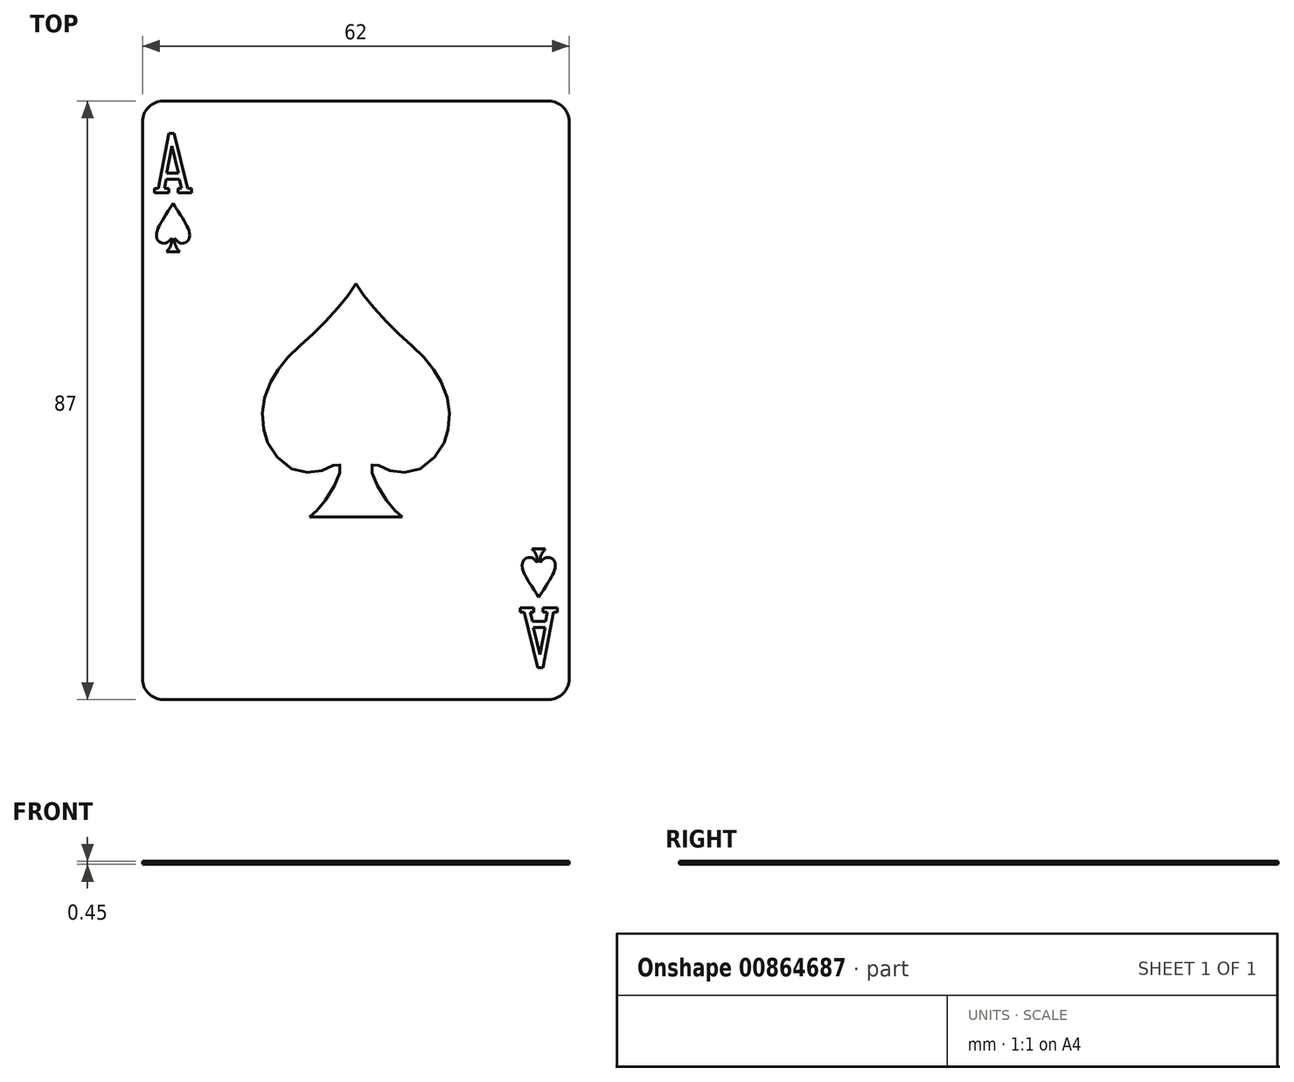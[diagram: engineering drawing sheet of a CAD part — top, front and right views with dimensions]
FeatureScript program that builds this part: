
annotation { "Feature Type Name" : "Feature", "Feature Type Description" : "" }
export const myFeature = defineFeature(function(context is Context, id is Id, definition is map)
    precondition{}
    {
        {
            var Q0;
            Q0=qCreatedBy(makeId("Top.planeOp"),FACE);
            var sketch = newSketch(context, id + "F0", { "sketchPlane" : qUnion([Q0])});
            skLineSegment(sketch, "E0.bottom", {"start": v(0, 0) * mm, "end": v(62, 0) * mm});
            skLineSegment(sketch, "E0.top", {"start": v(0, 87) * mm, "end": v(62, 87) * mm});
            skLineSegment(sketch, "E0.left", {"start": v(0, 0) * mm, "end": v(0, 87) * mm});
            skLineSegment(sketch, "E0.right", {"start": v(62, 0) * mm, "end": v(62, 87) * mm});
            skSolve(sketch);
        }
        {
            var Q0;
            Q0=makeQuery(id+"F0.imprint","IMPRINT",FACE,{"disambiguationData":[TD([[makeQuery(id+"F0.imprint","IMPRINT",EDGE,{"derivedFrom":sQuery(id+"F0.wireOp",EDGE,"E0.bottom")}),1.0]])]});
            extrude(context, id + "F1", {"entities" : qUnion([Q0]), "depth" : .45 * mm, "offsetDistance" : 25 * mm});
        }
        {
            var Q0;
            Q0=makeQuery(id+"F1.opExtrude","SWEPT_EDGE",EDGE,{"disambiguationData":[OSD([sQuery(id+"F0.wireOp",EDGE,"E0.top"),sQuery(id+"F0.wireOp",EDGE,"E0.right")])]});
            var Q1;
            Q1=makeQuery(id+"F1.opExtrude","SWEPT_EDGE",EDGE,{"disambiguationData":[OSD([sQuery(id+"F0.wireOp",EDGE,"E0.top"),sQuery(id+"F0.wireOp",EDGE,"E0.left")])]});
            var Q2;
            Q2=makeQuery(id+"F1.opExtrude","SWEPT_EDGE",EDGE,{"disambiguationData":[OSD([sQuery(id+"F0.wireOp",EDGE,"E0.bottom"),sQuery(id+"F0.wireOp",EDGE,"E0.right")])]});
            var Q3;
            Q3=makeQuery(id+"F1.opExtrude","SWEPT_EDGE",EDGE,{"disambiguationData":[OSD([sQuery(id+"F0.wireOp",EDGE,"E0.bottom"),sQuery(id+"F0.wireOp",EDGE,"E0.left")])]});
            fillet(context, id + "F2", {"entities" : qUnion([Q0, Q1, Q2, Q3]), "radius" : 3 * mm, "tangentPropagation" : true, "allowEdgeOverflow" : false});
        }
        {
            var Q0;
            Q0=makeQuery(id+"F1.opExtrude","CAP_FACE",FACE,{"disambiguationData":[OSD([sQuery(id+"F0.wireOp",EDGE,"E0.bottom"),sQuery(id+"F0.wireOp",EDGE,"E0.top"),sQuery(id+"F0.wireOp",EDGE,"E0.left"),sQuery(id+"F0.wireOp",EDGE,"E0.right")])],"isStart":false});
            var sketch = newSketch(context, id + "F3", { "sketchPlane" : qUnion([Q0])});
            skLineSegment(sketch, "E1", {"start": v(3.8, 82.32) * mm, "end": v(4.61, 82.32) * mm});
            skLineSegment(sketch, "E2", {"start": v(4.61, 82.32) * mm, "end": v(6.53, 74.3) * mm});
            skLineSegment(sketch, "E3", {"start": v(6.53, 74.3) * mm, "end": v(7.12, 74.3) * mm});
            skLineSegment(sketch, "E4", {"start": v(7.12, 74.3) * mm, "end": v(7.12, 73.68) * mm});
            skLineSegment(sketch, "E5", {"start": v(7.12, 73.68) * mm, "end": v(5.13, 73.68) * mm});
            skLineSegment(sketch, "E6", {"start": v(5.13, 73.68) * mm, "end": v(5.13, 74.3) * mm});
            skLineSegment(sketch, "E7", {"start": v(5.13, 74.3) * mm, "end": v(5.66, 74.3) * mm});
            skLineSegment(sketch, "E8", {"start": v(5.66, 74.3) * mm, "end": v(5.34, 75.64) * mm});
            skLineSegment(sketch, "E9", {"start": v(5.2, 76.53) * mm, "end": v(4.27, 80.45) * mm});
            skLineSegment(sketch, "E10", {"start": v(4.27, 80.45) * mm, "end": v(4.27, 76.53) * mm, "construction": true});
            skLineSegment(sketch, "E11", {"start": v(4.27, 76.53) * mm, "end": v(5.2, 76.53) * mm});
            skLineSegment(sketch, "E12", {"start": v(3.8, 82.32) * mm, "end": v(2.3, 74.3) * mm});
            skLineSegment(sketch, "E13", {"start": v(2.3, 74.3) * mm, "end": v(1.73, 74.3) * mm});
            skLineSegment(sketch, "E14", {"start": v(1.73, 74.3) * mm, "end": v(1.73, 73.68) * mm});
            skLineSegment(sketch, "E15", {"start": v(1.73, 73.68) * mm, "end": v(3.8, 73.68) * mm});
            skLineSegment(sketch, "E16", {"start": v(3.8, 73.68) * mm, "end": v(3.8, 74.3) * mm});
            skLineSegment(sketch, "E17", {"start": v(3.8, 74.3) * mm, "end": v(3.16, 74.3) * mm});
            skLineSegment(sketch, "E18", {"start": v(3.16, 74.3) * mm, "end": v(3.41, 75.64) * mm});
            skLineSegment(sketch, "E19", {"start": v(3.41, 75.64) * mm, "end": v(5.34, 75.64) * mm});
            skLineSegment(sketch, "E20", {"start": v(4.27, 80.45) * mm, "end": v(3.53, 76.53) * mm});
            skLineSegment(sketch, "E21", {"start": v(3.53, 76.53) * mm, "end": v(4.27, 76.53) * mm});
            skFitSpline(sketch, "E22", {"points": [v(4.44, 72.15) * mm, v(3.33, 70.36) * mm, v(2.7, 69.36) * mm, v(2.29, 68.57) * mm, v(2.1, 68.02) * mm, v(2.04, 67.43) * mm, v(2.09, 67.06) * mm, v(2.23, 66.78) * mm, v(2.46, 66.55) * mm, v(2.76, 66.38) * mm, v(3.05, 66.32) * mm, v(3.37, 66.35) * mm, v(3.74, 66.56) * mm, v(4.03, 66.86) * mm, v(4.24, 67.04) * mm], "startDerivative": vector(-8.43, -13.66) * mm, "endDerivative": vector(4.01, 3.14) * mm});
            skFitSpline(sketch, "E23", {"points": [v(4.24, 67.04) * mm, v(4.24, 66.65) * mm, v(4.19, 66.33) * mm, v(4.04, 65.9) * mm, v(3.86, 65.56) * mm, v(3.48, 65.1) * mm], "startDerivative": vector(0.06, -2.1) * mm, "endDerivative": vector(-1.77, -2.06) * mm});
            skLineSegment(sketch, "E24", {"start": v(4.44, 72.15) * mm, "end": v(4.44, 65.1) * mm, "construction": true});
            skLineSegment(sketch, "E25", {"start": v(4.44, 65.1) * mm, "end": v(3.48, 65.1) * mm});
            skFitSpline(sketch, "E26.MirrorCS", {"points": [v(4.44, 72.15) * mm, v(5.55, 70.36) * mm, v(6.17, 69.36) * mm, v(6.6, 68.57) * mm, v(6.77, 68.02) * mm, v(6.84, 67.43) * mm, v(6.79, 67.06) * mm, v(6.65, 66.78) * mm, v(6.42, 66.55) * mm, v(6.12, 66.38) * mm, v(5.83, 66.32) * mm, v(5.5, 66.35) * mm, v(5.14, 66.56) * mm, v(4.84, 66.86) * mm, v(4.64, 67.04) * mm], "startDerivative": vector(8.43, -13.66) * mm, "endDerivative": vector(-4.01, 3.14) * mm});
            skFitSpline(sketch, "E27.MirrorCS", {"points": [v(4.64, 67.04) * mm, v(4.64, 66.65) * mm, v(4.7, 66.33) * mm, v(4.84, 65.9) * mm, v(5.02, 65.56) * mm, v(5.4, 65.1) * mm], "startDerivative": vector(-0.06, -2.1) * mm, "endDerivative": vector(1.77, -2.06) * mm});
            skLineSegment(sketch, "E28.MirrorCS", {"start": v(4.44, 65.1) * mm, "end": v(5.4, 65.1) * mm});
            skLineSegment(sketch, "E29", {"start": v(31, 60.45) * mm, "end": v(31, 26.55) * mm, "construction": true});
            skLineSegment(sketch, "E30", {"start": v(31, 26.55) * mm, "end": v(24.25, 26.55) * mm});
            skFitSpline(sketch, "E31", {"points": [v(24.25, 26.55) * mm, v(24.65, 26.85) * mm, v(25.45, 27.6) * mm, v(26.17, 28.4) * mm, v(27.38, 30.2) * mm, v(28.34, 32.14) * mm, v(28.67, 33.11) * mm, v(28.77, 33.72) * mm, v(28.7, 34.05) * mm, v(28.5, 34.26) * mm, v(28.23, 34.26) * mm, v(27.64, 33.98) * mm, v(26.5, 33.48) * mm, v(25.17, 33.08) * mm, v(23.3, 33.1) * mm, v(21.34, 33.73) * mm, v(19.3, 35.6) * mm, v(18.1, 37.48) * mm, v(17.65, 38.98) * mm, v(17.45, 40.78) * mm, v(17.53, 42.9) * mm, v(17.89, 44.5) * mm, v(18.84, 46.62) * mm, v(19.65, 47.87) * mm, v(20.8, 49.35) * mm, v(22.24, 50.86) * mm, v(24.08, 52.59) * mm, v(25.67, 54.05) * mm, v(27.56, 56.04) * mm, v(29.08, 57.82) * mm, v(30.15, 59.16) * mm, v(31, 60.45) * mm], "startDerivative": vector(19.76, 13.7) * mm, "endDerivative": vector(24.95, 39.9) * mm});
            skFitSpline(sketch, "E32.MirrorCS", {"points": [v(37.75, 26.55) * mm, v(37.35, 26.85) * mm, v(36.55, 27.6) * mm, v(35.83, 28.4) * mm, v(34.62, 30.2) * mm, v(33.66, 32.14) * mm, v(33.33, 33.11) * mm, v(33.23, 33.72) * mm, v(33.3, 34.05) * mm, v(33.5, 34.26) * mm, v(33.77, 34.26) * mm, v(34.36, 33.98) * mm, v(35.5, 33.48) * mm, v(36.83, 33.08) * mm, v(38.7, 33.1) * mm, v(40.66, 33.73) * mm, v(42.7, 35.6) * mm, v(43.9, 37.48) * mm, v(44.35, 38.98) * mm, v(44.55, 40.78) * mm, v(44.47, 42.9) * mm, v(44.11, 44.5) * mm, v(43.16, 46.62) * mm, v(42.35, 47.87) * mm, v(41.2, 49.35) * mm, v(39.76, 50.86) * mm, v(37.92, 52.59) * mm, v(36.33, 54.05) * mm, v(34.44, 56.04) * mm, v(32.92, 57.82) * mm, v(31.85, 59.16) * mm, v(31, 60.45) * mm], "startDerivative": vector(-19.76, 13.7) * mm, "endDerivative": vector(-24.95, 39.9) * mm});
            skLineSegment(sketch, "E33", {"start": v(37.75, 26.55) * mm, "end": v(31, 26.55) * mm});
            skLineSegment(sketch, "E34", {"start": v(0, 43.5) * mm, "end": v(62, 43.5) * mm, "construction": true});
            skLineSegment(sketch, "E35.1.0", {"start": v(60.27, 13.32) * mm, "end": v(58.2, 13.32) * mm});
            skLineSegment(sketch, "E35.1.1", {"start": v(54.88, 13.32) * mm, "end": v(56.87, 13.32) * mm});
            skLineSegment(sketch, "E35.1.2", {"start": v(56.8, 10.47) * mm, "end": v(57.73, 6.55) * mm});
            skLineSegment(sketch, "E35.1.3", {"start": v(57.73, 6.55) * mm, "end": v(58.47, 10.47) * mm});
            skLineSegment(sketch, "E35.1.4", {"start": v(58.59, 11.36) * mm, "end": v(56.66, 11.36) * mm});
            skLineSegment(sketch, "E35.1.5", {"start": v(57.39, 4.68) * mm, "end": v(55.47, 12.7) * mm});
            skLineSegment(sketch, "E35.1.6", {"start": v(57.73, 6.55) * mm, "end": v(57.73, 10.47) * mm, "construction": true});
            skLineSegment(sketch, "E35.1.7", {"start": v(58.2, 4.68) * mm, "end": v(59.7, 12.7) * mm});
            skLineSegment(sketch, "E35.1.8", {"start": v(57.56, 14.85) * mm, "end": v(57.56, 21.9) * mm, "construction": true});
            skLineSegment(sketch, "E35.1.9", {"start": v(57.73, 10.47) * mm, "end": v(56.8, 10.47) * mm});
            skLineSegment(sketch, "E35.1.10", {"start": v(58.2, 4.68) * mm, "end": v(57.39, 4.68) * mm});
            skLineSegment(sketch, "E35.1.11", {"start": v(59.7, 12.7) * mm, "end": v(60.27, 12.7) * mm});
            skLineSegment(sketch, "E35.1.12", {"start": v(58.2, 13.32) * mm, "end": v(58.2, 12.7) * mm});
            skLineSegment(sketch, "E35.1.13", {"start": v(58.2, 12.7) * mm, "end": v(58.84, 12.7) * mm});
            skLineSegment(sketch, "E35.1.14", {"start": v(55.47, 12.7) * mm, "end": v(54.88, 12.7) * mm});
            skLineSegment(sketch, "E35.1.15", {"start": v(56.87, 13.32) * mm, "end": v(56.87, 12.7) * mm});
            skLineSegment(sketch, "E35.1.16", {"start": v(54.88, 12.7) * mm, "end": v(54.88, 13.32) * mm});
            skLineSegment(sketch, "E35.1.17", {"start": v(58.47, 10.47) * mm, "end": v(57.73, 10.47) * mm});
            skLineSegment(sketch, "E35.1.18", {"start": v(58.84, 12.7) * mm, "end": v(58.59, 11.36) * mm});
            skLineSegment(sketch, "E35.1.19", {"start": v(60.27, 12.7) * mm, "end": v(60.27, 13.32) * mm});
            skLineSegment(sketch, "E35.1.20", {"start": v(56.87, 12.7) * mm, "end": v(56.34, 12.7) * mm});
            skLineSegment(sketch, "E35.1.21", {"start": v(56.34, 12.7) * mm, "end": v(56.66, 11.36) * mm});
            skLineSegment(sketch, "E35.1.22", {"start": v(57.56, 21.9) * mm, "end": v(58.52, 21.9) * mm});
            skLineSegment(sketch, "E35.1.23", {"start": v(57.56, 21.9) * mm, "end": v(56.6, 21.9) * mm});
            skPoint(sketch, "E35.center", {"position": v(31.8, 43.83) * mm});
            skFitSpline(sketch, "E36", {"points": [v(57.56, 14.85) * mm, v(58.67, 16.64) * mm, v(59.3, 17.64) * mm, v(59.71, 18.43) * mm, v(59.9, 18.98) * mm, v(59.96, 19.57) * mm, v(59.91, 19.94) * mm, v(59.77, 20.22) * mm, v(59.54, 20.45) * mm, v(59.24, 20.62) * mm, v(58.95, 20.68) * mm, v(58.63, 20.65) * mm, v(58.26, 20.44) * mm, v(57.97, 20.14) * mm, v(57.76, 19.96) * mm], "startDerivative": vector(8.43, 13.66) * mm, "endDerivative": vector(-4.01, -3.14) * mm});
            skFitSpline(sketch, "E37", {"points": [v(57.76, 19.96) * mm, v(57.76, 20.35) * mm, v(57.81, 20.67) * mm, v(57.96, 21.1) * mm, v(58.14, 21.44) * mm, v(58.52, 21.9) * mm], "startDerivative": vector(-0.06, 2.1) * mm, "endDerivative": vector(1.77, 2.06) * mm});
            skFitSpline(sketch, "E38.MirrorCS", {"points": [v(57.56, 14.85) * mm, v(56.45, 16.64) * mm, v(55.83, 17.64) * mm, v(55.4, 18.43) * mm, v(55.23, 18.98) * mm, v(55.16, 19.57) * mm, v(55.21, 19.94) * mm, v(55.35, 20.22) * mm, v(55.58, 20.45) * mm, v(55.88, 20.62) * mm, v(56.17, 20.68) * mm, v(56.5, 20.65) * mm, v(56.86, 20.44) * mm, v(57.16, 20.14) * mm, v(57.36, 19.96) * mm], "startDerivative": vector(-8.43, 13.66) * mm, "endDerivative": vector(4.01, -3.14) * mm});
            skFitSpline(sketch, "E39.MirrorCS", {"points": [v(57.36, 19.96) * mm, v(57.36, 20.35) * mm, v(57.3, 20.67) * mm, v(57.16, 21.1) * mm, v(56.98, 21.44) * mm, v(56.6, 21.9) * mm], "startDerivative": vector(0.06, 2.1) * mm, "endDerivative": vector(-1.77, 2.06) * mm});
            skSolve(sketch);
        }
        {
            var Q0;
            Q0 = qSketchRegion(id + "F3", true);
            extrude(context, id + "F4", {"entities" : qUnion([Q0]), "operationType" : NewBodyOperationType.REMOVE, "oppositeDirection" : true, "depth" : .1 * mm, "offsetDistance" : 25 * mm});
        }
    });
